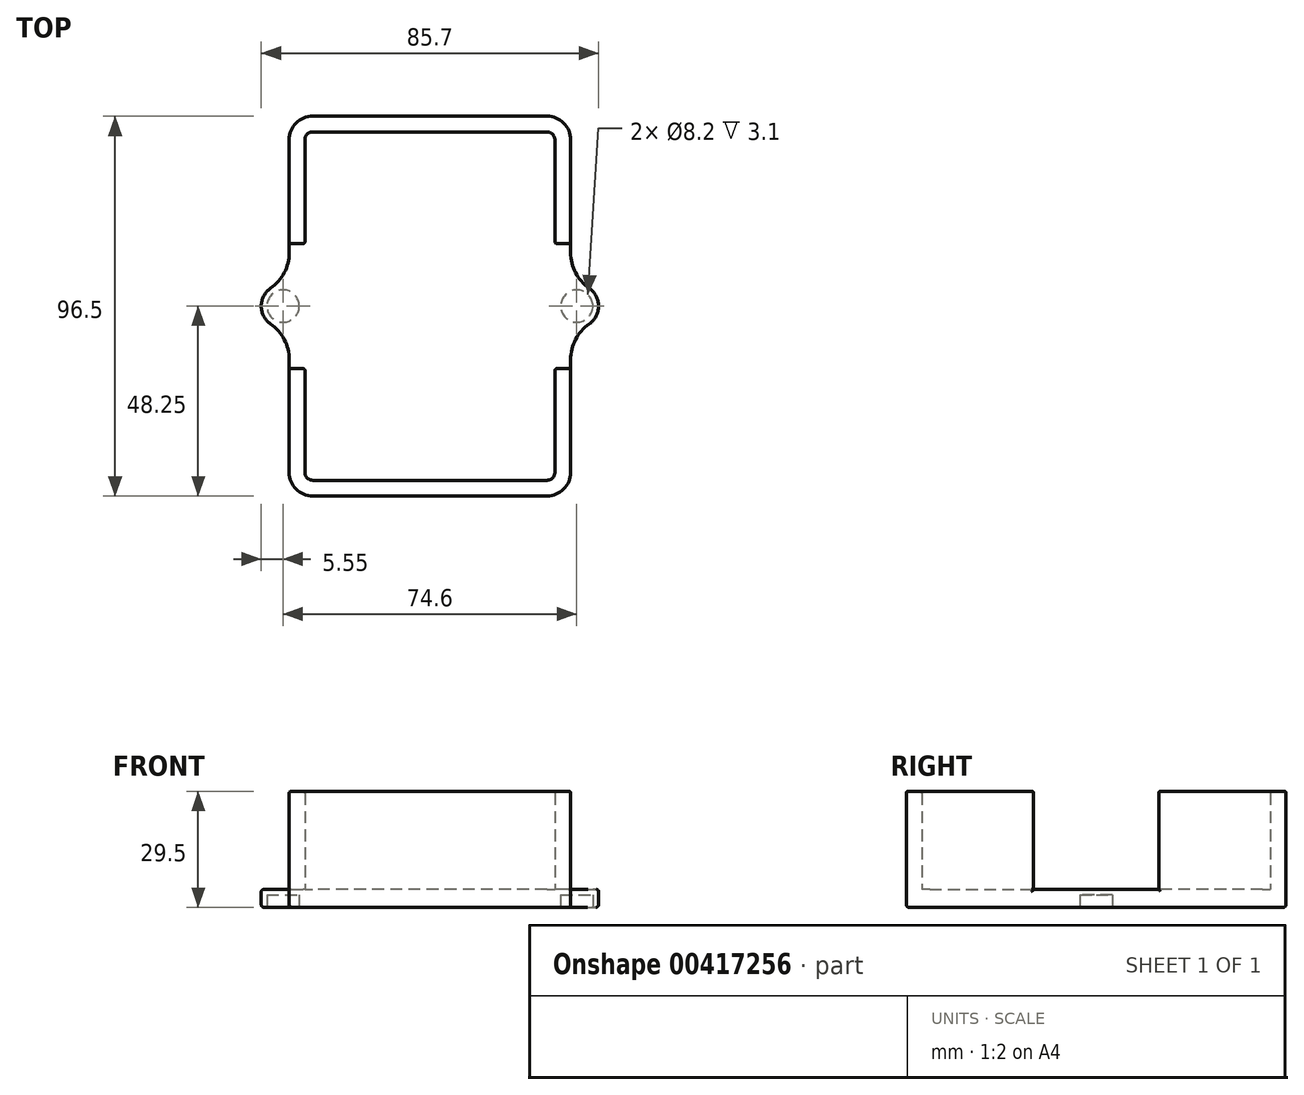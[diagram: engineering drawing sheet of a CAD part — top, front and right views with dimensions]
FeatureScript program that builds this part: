
annotation { "Feature Type Name" : "Feature", "Feature Type Description" : "" }
export const myFeature = defineFeature(function(context is Context, id is Id, definition is map)
    precondition{}
    {
        {
            var Q0;
            Q0=qCreatedBy(makeId("Top.planeOp"),FACE);
            var sketch = newSketch(context, id + "F0", { "sketchPlane" : qUnion([Q0])});
            skLineSegment(sketch, "E0", {"start": v(35.75, 42.25) * mm, "end": v(35.75, 13.59) * mm});
            skArc(sketch, "E1", {"start": v(35.75, 13.59) * mm, "mid": v(37, 8.5) * mm, "end": v(40.47, 4.56) * mm});
            skArc(sketch, "E2", {"start": v(40.47, 4.56) * mm, "mid": v(42.85, 0) * mm, "end": v(40.47, -4.56) * mm});
            skArc(sketch, "E3", {"start": v(40.47, -4.56) * mm, "mid": v(37, -8.5) * mm, "end": v(35.75, -13.59) * mm});
            skLineSegment(sketch, "E4", {"start": v(35.75, -13.59) * mm, "end": v(35.75, -42.25) * mm});
            skArc(sketch, "E5", {"start": v(35.75, -42.25) * mm, "mid": v(34, -46.5) * mm, "end": v(29.75, -48.25) * mm});
            skLineSegment(sketch, "E6", {"start": v(29.75, -48.25) * mm, "end": v(-29.75, -48.25) * mm});
            skArc(sketch, "E7", {"start": v(-29.75, -48.25) * mm, "mid": v(-34, -46.5) * mm, "end": v(-35.75, -42.25) * mm});
            skLineSegment(sketch, "E8", {"start": v(-35.75, -42.25) * mm, "end": v(-35.75, -13.59) * mm});
            skArc(sketch, "E9", {"start": v(-35.75, -13.59) * mm, "mid": v(-37, -8.5) * mm, "end": v(-40.47, -4.56) * mm});
            skArc(sketch, "E10", {"start": v(-40.47, -4.56) * mm, "mid": v(-42.85, 0) * mm, "end": v(-40.47, 4.56) * mm});
            skArc(sketch, "E11", {"start": v(-40.47, 4.56) * mm, "mid": v(-37, 8.5) * mm, "end": v(-35.75, 13.59) * mm});
            skLineSegment(sketch, "E12", {"start": v(-35.75, 13.59) * mm, "end": v(-35.75, 42.25) * mm});
            skArc(sketch, "E13", {"start": v(-35.75, 42.25) * mm, "mid": v(-34, 46.5) * mm, "end": v(-29.75, 48.25) * mm});
            skLineSegment(sketch, "E14", {"start": v(-29.75, 48.25) * mm, "end": v(29.75, 48.25) * mm});
            skArc(sketch, "E15", {"start": v(29.75, 48.25) * mm, "mid": v(34, 46.5) * mm, "end": v(35.75, 42.25) * mm});
            skSolve(sketch);
        }
        {
            var Q0;
            Q0=qSketchRegion(id+"F0",true);
            extrude(context, id + "F1", {"entities" : qUnion([Q0]), "depth" : 4.5 * mm});
        }
        {
            var Q0;
            Q0=makeQuery(id+"F1.opExtrude","CAP_FACE",FACE,{"disambiguationData":[OSD([sQuery(id+"F0.wireOp",EDGE,"E0"),sQuery(id+"F0.wireOp",EDGE,"E1"),sQuery(id+"F0.wireOp",EDGE,"E2"),sQuery(id+"F0.wireOp",EDGE,"E3"),sQuery(id+"F0.wireOp",EDGE,"E4"),sQuery(id+"F0.wireOp",EDGE,"E5"),sQuery(id+"F0.wireOp",EDGE,"E6"),sQuery(id+"F0.wireOp",EDGE,"E7"),sQuery(id+"F0.wireOp",EDGE,"E8"),sQuery(id+"F0.wireOp",EDGE,"E9"),sQuery(id+"F0.wireOp",EDGE,"E10"),sQuery(id+"F0.wireOp",EDGE,"E11"),sQuery(id+"F0.wireOp",EDGE,"E12"),sQuery(id+"F0.wireOp",EDGE,"E13"),sQuery(id+"F0.wireOp",EDGE,"E14"),sQuery(id+"F0.wireOp",EDGE,"E15")])],"isStart":true});
            var sketch = newSketch(context, id + "F2", { "sketchPlane" : qUnion([Q0])});
            skCircle(sketch, "E16", {"center": v(-37.3, 0) * mm, "radius": 4.1 * mm});
            skCircle(sketch, "E17", {"center": v(37.3, 0) * mm, "radius": 4.1 * mm});
            skSolve(sketch);
        }
        {
            var Q0;
            Q0=qSketchRegion(id+"F2",true);
            extrude(context, id + "F3", {"entities" : qUnion([Q0]), "operationType" : NewBodyOperationType.REMOVE, "oppositeDirection" : true, "depth" : 3.1 * mm});
        }
        {
            var Q0;
            Q0=makeQuery(id+"F1.opExtrude","CAP_FACE",FACE,{"disambiguationData":[OSD([sQuery(id+"F0.wireOp",EDGE,"E0"),sQuery(id+"F0.wireOp",EDGE,"E1"),sQuery(id+"F0.wireOp",EDGE,"E2"),sQuery(id+"F0.wireOp",EDGE,"E3"),sQuery(id+"F0.wireOp",EDGE,"E4"),sQuery(id+"F0.wireOp",EDGE,"E5"),sQuery(id+"F0.wireOp",EDGE,"E6"),sQuery(id+"F0.wireOp",EDGE,"E7"),sQuery(id+"F0.wireOp",EDGE,"E8"),sQuery(id+"F0.wireOp",EDGE,"E9"),sQuery(id+"F0.wireOp",EDGE,"E10"),sQuery(id+"F0.wireOp",EDGE,"E11"),sQuery(id+"F0.wireOp",EDGE,"E12"),sQuery(id+"F0.wireOp",EDGE,"E13"),sQuery(id+"F0.wireOp",EDGE,"E14"),sQuery(id+"F0.wireOp",EDGE,"E15")])],"isStart":false});
            var sketch = newSketch(context, id + "F4", { "sketchPlane" : qUnion([Q0])});
            skArc(sketch, "E18", {"start": v(-35.75, 16.39) * mm, "mid": v(-35.6, 16.03) * mm, "end": v(-35.25, 15.89) * mm});
            skLineSegment(sketch, "E19", {"start": v(-35.25, 15.89) * mm, "end": v(-32.25, 15.89) * mm});
            skArc(sketch, "E20", {"start": v(-32.25, 15.89) * mm, "mid": v(-31.9, 16.03) * mm, "end": v(-31.75, 16.39) * mm});
            skLineSegment(sketch, "E21", {"start": v(-31.75, 16.39) * mm, "end": v(-31.75, 42.25) * mm});
            skArc(sketch, "E22", {"start": v(-31.75, 42.25) * mm, "mid": v(-31.16, 43.66) * mm, "end": v(-29.75, 44.25) * mm});
            skLineSegment(sketch, "E23", {"start": v(-29.75, 44.25) * mm, "end": v(29.75, 44.25) * mm});
            skArc(sketch, "E24", {"start": v(29.75, 44.25) * mm, "mid": v(31.16, 43.66) * mm, "end": v(31.75, 42.25) * mm});
            skLineSegment(sketch, "E25", {"start": v(31.75, 42.25) * mm, "end": v(31.75, 16.39) * mm});
            skArc(sketch, "E26", {"start": v(31.75, 16.39) * mm, "mid": v(31.9, 16.03) * mm, "end": v(32.25, 15.89) * mm});
            skLineSegment(sketch, "E27", {"start": v(32.25, 15.89) * mm, "end": v(35.25, 15.89) * mm});
            skArc(sketch, "E28", {"start": v(35.25, 15.89) * mm, "mid": v(35.6, 16.03) * mm, "end": v(35.75, 16.39) * mm});
            skLineSegment(sketch, "E29", {"start": v(35.75, 16.39) * mm, "end": v(35.75, 42.25) * mm});
            skArc(sketch, "E30", {"start": v(35.75, 42.25) * mm, "mid": v(34, 46.5) * mm, "end": v(29.75, 48.25) * mm});
            skLineSegment(sketch, "E31", {"start": v(29.75, 48.25) * mm, "end": v(-29.75, 48.25) * mm});
            skArc(sketch, "E32", {"start": v(-29.75, 48.25) * mm, "mid": v(-34, 46.5) * mm, "end": v(-35.75, 42.25) * mm});
            skLineSegment(sketch, "E33", {"start": v(-35.75, 42.25) * mm, "end": v(-35.75, 16.39) * mm});
            skArc(sketch, "E34", {"start": v(35.75, -16.39) * mm, "mid": v(35.6, -16.03) * mm, "end": v(35.25, -15.89) * mm});
            skLineSegment(sketch, "E35", {"start": v(35.25, -15.89) * mm, "end": v(32.25, -15.89) * mm});
            skArc(sketch, "E36", {"start": v(32.25, -15.89) * mm, "mid": v(31.9, -16.03) * mm, "end": v(31.75, -16.39) * mm});
            skLineSegment(sketch, "E37", {"start": v(31.75, -16.39) * mm, "end": v(31.75, -42.25) * mm});
            skArc(sketch, "E38", {"start": v(31.75, -42.25) * mm, "mid": v(31.16, -43.66) * mm, "end": v(29.75, -44.25) * mm});
            skLineSegment(sketch, "E39", {"start": v(29.75, -44.25) * mm, "end": v(-29.75, -44.25) * mm});
            skArc(sketch, "E40", {"start": v(-29.75, -44.25) * mm, "mid": v(-31.16, -43.66) * mm, "end": v(-31.75, -42.25) * mm});
            skLineSegment(sketch, "E41", {"start": v(-31.75, -42.25) * mm, "end": v(-31.75, -16.39) * mm});
            skArc(sketch, "E42", {"start": v(-31.75, -16.39) * mm, "mid": v(-31.9, -16.03) * mm, "end": v(-32.25, -15.89) * mm});
            skLineSegment(sketch, "E43", {"start": v(-32.25, -15.89) * mm, "end": v(-35.25, -15.89) * mm});
            skArc(sketch, "E44", {"start": v(-35.25, -15.89) * mm, "mid": v(-35.6, -16.03) * mm, "end": v(-35.75, -16.39) * mm});
            skLineSegment(sketch, "E45", {"start": v(-35.75, -16.39) * mm, "end": v(-35.75, -42.25) * mm});
            skArc(sketch, "E46", {"start": v(-35.75, -42.25) * mm, "mid": v(-34, -46.5) * mm, "end": v(-29.75, -48.25) * mm});
            skLineSegment(sketch, "E47", {"start": v(-29.75, -48.25) * mm, "end": v(29.75, -48.25) * mm});
            skArc(sketch, "E48", {"start": v(29.75, -48.25) * mm, "mid": v(34, -46.5) * mm, "end": v(35.75, -42.25) * mm});
            skLineSegment(sketch, "E49", {"start": v(35.75, -42.25) * mm, "end": v(35.75, -16.39) * mm});
            skSolve(sketch);
        }
        {
            var Q0;
            Q0=qSketchRegion(id+"F4",true);
            extrude(context, id + "F5", {"entities" : qUnion([Q0]), "operationType" : NewBodyOperationType.ADD, "depth" : 25 * mm});
        }
        {
            var Q0;
            Q0=makeQuery(id+"F1.opExtrude","CAP_EDGE",EDGE,{"disambiguationData":[OSD([sQuery(id+"F0.wireOp",EDGE,"E14")])],"isStart":true});
            var Q1;
            Q1=makeQuery(id+"F1.opExtrude","CAP_EDGE",EDGE,{"disambiguationData":[OSD([sQuery(id+"F0.wireOp",EDGE,"E13")])],"isStart":true});
            var Q2;
            Q2=makeQuery(id+"F1.opExtrude","CAP_EDGE",EDGE,{"disambiguationData":[OSD([sQuery(id+"F0.wireOp",EDGE,"E12")])],"isStart":true});
            var Q3;
            Q3=makeQuery(id+"F1.opExtrude","CAP_EDGE",EDGE,{"disambiguationData":[OSD([sQuery(id+"F0.wireOp",EDGE,"E11")])],"isStart":true});
            var Q4;
            Q4=makeQuery(id+"F1.opExtrude","CAP_EDGE",EDGE,{"disambiguationData":[OSD([sQuery(id+"F0.wireOp",EDGE,"E10")])],"isStart":true});
            var Q5;
            Q5=makeQuery(id+"F1.opExtrude","CAP_EDGE",EDGE,{"disambiguationData":[OSD([sQuery(id+"F0.wireOp",EDGE,"E9")])],"isStart":true});
            var Q6;
            Q6=makeQuery(id+"F1.opExtrude","CAP_EDGE",EDGE,{"disambiguationData":[OSD([sQuery(id+"F0.wireOp",EDGE,"E8")])],"isStart":true});
            var Q7;
            Q7=makeQuery(id+"F1.opExtrude","CAP_EDGE",EDGE,{"disambiguationData":[OSD([sQuery(id+"F0.wireOp",EDGE,"E7")])],"isStart":true});
            var Q8;
            Q8=makeQuery(id+"F1.opExtrude","CAP_EDGE",EDGE,{"disambiguationData":[OSD([sQuery(id+"F0.wireOp",EDGE,"E6")])],"isStart":true});
            var Q9;
            Q9=makeQuery(id+"F1.opExtrude","CAP_EDGE",EDGE,{"disambiguationData":[OSD([sQuery(id+"F0.wireOp",EDGE,"E5")])],"isStart":true});
            var Q10;
            Q10=makeQuery(id+"F1.opExtrude","CAP_EDGE",EDGE,{"disambiguationData":[OSD([sQuery(id+"F0.wireOp",EDGE,"E4")])],"isStart":true});
            var Q11;
            Q11=makeQuery(id+"F1.opExtrude","CAP_EDGE",EDGE,{"disambiguationData":[OSD([sQuery(id+"F0.wireOp",EDGE,"E3")])],"isStart":true});
            var Q12;
            Q12=makeQuery(id+"F1.opExtrude","CAP_EDGE",EDGE,{"disambiguationData":[OSD([sQuery(id+"F0.wireOp",EDGE,"E2")])],"isStart":true});
            var Q13;
            Q13=makeQuery(id+"F1.opExtrude","CAP_EDGE",EDGE,{"disambiguationData":[OSD([sQuery(id+"F0.wireOp",EDGE,"E1")])],"isStart":true});
            var Q14;
            Q14=makeQuery(id+"F1.opExtrude","CAP_EDGE",EDGE,{"disambiguationData":[OSD([sQuery(id+"F0.wireOp",EDGE,"E0")])],"isStart":true});
            var Q15;
            Q15=makeQuery(id+"F1.opExtrude","CAP_EDGE",EDGE,{"disambiguationData":[OSD([sQuery(id+"F0.wireOp",EDGE,"E15")])],"isStart":true});
            fillet(context, id + "F6", {"entities" : qUnion([Q0, Q1, Q2, Q3, Q4, Q5, Q6, Q7, Q8, Q9, Q10, Q11, Q12, Q13, Q14, Q15]), "radius" : .7 * mm, "tangentPropagation" : true, "allowEdgeOverflow" : false});
        }
        {
            var Q0;
            Q0=makeQuery(id+"F5.opExtrude","CAP_EDGE",EDGE,{"disambiguationData":[OSD([sQuery(id+"F4.wireOp",EDGE,"E43")])],"isStart":false});
            var Q1;
            Q1=makeQuery(id+"F5.opExtrude","CAP_EDGE",EDGE,{"disambiguationData":[OSD([sQuery(id+"F4.wireOp",EDGE,"E42")])],"isStart":false});
            var Q2;
            Q2=makeQuery(id+"F5.opExtrude","CAP_EDGE",EDGE,{"disambiguationData":[OSD([sQuery(id+"F4.wireOp",EDGE,"E41")])],"isStart":false});
            var Q3;
            Q3=makeQuery(id+"F5.opExtrude","CAP_EDGE",EDGE,{"disambiguationData":[OSD([sQuery(id+"F4.wireOp",EDGE,"E44")])],"isStart":false});
            var Q4;
            Q4=makeQuery(id+"F5.opExtrude","CAP_EDGE",EDGE,{"disambiguationData":[OSD([sQuery(id+"F4.wireOp",EDGE,"E45")])],"isStart":false});
            var Q5;
            Q5=makeQuery(id+"F5.opExtrude","CAP_EDGE",EDGE,{"disambiguationData":[OSD([sQuery(id+"F4.wireOp",EDGE,"E46")])],"isStart":false});
            var Q6;
            Q6=makeQuery(id+"F5.opExtrude","CAP_EDGE",EDGE,{"disambiguationData":[OSD([sQuery(id+"F4.wireOp",EDGE,"E40")])],"isStart":false});
            var Q7;
            Q7=makeQuery(id+"F5.opExtrude","CAP_EDGE",EDGE,{"disambiguationData":[OSD([sQuery(id+"F4.wireOp",EDGE,"E39")])],"isStart":false});
            var Q8;
            Q8=makeQuery(id+"F5.opExtrude","CAP_EDGE",EDGE,{"disambiguationData":[OSD([sQuery(id+"F4.wireOp",EDGE,"E47")])],"isStart":false});
            var Q9;
            Q9=makeQuery(id+"F5.opExtrude","CAP_EDGE",EDGE,{"disambiguationData":[OSD([sQuery(id+"F4.wireOp",EDGE,"E48")])],"isStart":false});
            var Q10;
            Q10=makeQuery(id+"F5.opExtrude","CAP_EDGE",EDGE,{"disambiguationData":[OSD([sQuery(id+"F4.wireOp",EDGE,"E38")])],"isStart":false});
            var Q11;
            Q11=makeQuery(id+"F5.opExtrude","CAP_EDGE",EDGE,{"disambiguationData":[OSD([sQuery(id+"F4.wireOp",EDGE,"E37")])],"isStart":false});
            var Q12;
            Q12=makeQuery(id+"F5.opExtrude","CAP_EDGE",EDGE,{"disambiguationData":[OSD([sQuery(id+"F4.wireOp",EDGE,"E49")])],"isStart":false});
            var Q13;
            Q13=makeQuery(id+"F5.opExtrude","CAP_EDGE",EDGE,{"disambiguationData":[OSD([sQuery(id+"F4.wireOp",EDGE,"E34")])],"isStart":false});
            var Q14;
            Q14=makeQuery(id+"F5.opExtrude","CAP_EDGE",EDGE,{"disambiguationData":[OSD([sQuery(id+"F4.wireOp",EDGE,"E35")])],"isStart":false});
            var Q15;
            Q15=makeQuery(id+"F5.opExtrude","CAP_EDGE",EDGE,{"disambiguationData":[OSD([sQuery(id+"F4.wireOp",EDGE,"E36")])],"isStart":false});
            var Q16;
            Q16=makeQuery(id+"F5.opExtrude","CAP_EDGE",EDGE,{"disambiguationData":[OSD([sQuery(id+"F4.wireOp",EDGE,"E27")])],"isStart":false});
            var Q17;
            Q17=makeQuery(id+"F5.opExtrude","CAP_EDGE",EDGE,{"disambiguationData":[OSD([sQuery(id+"F4.wireOp",EDGE,"E26")])],"isStart":false});
            var Q18;
            Q18=makeQuery(id+"F5.opExtrude","CAP_EDGE",EDGE,{"disambiguationData":[OSD([sQuery(id+"F4.wireOp",EDGE,"E25")])],"isStart":false});
            var Q19;
            Q19=makeQuery(id+"F5.opExtrude","CAP_EDGE",EDGE,{"disambiguationData":[OSD([sQuery(id+"F4.wireOp",EDGE,"E28")])],"isStart":false});
            var Q20;
            Q20=makeQuery(id+"F5.opExtrude","CAP_EDGE",EDGE,{"disambiguationData":[OSD([sQuery(id+"F4.wireOp",EDGE,"E29")])],"isStart":false});
            var Q21;
            Q21=makeQuery(id+"F5.opExtrude","CAP_EDGE",EDGE,{"disambiguationData":[OSD([sQuery(id+"F4.wireOp",EDGE,"E30")])],"isStart":false});
            var Q22;
            Q22=makeQuery(id+"F5.opExtrude","CAP_EDGE",EDGE,{"disambiguationData":[OSD([sQuery(id+"F4.wireOp",EDGE,"E24")])],"isStart":false});
            var Q23;
            Q23=makeQuery(id+"F5.opExtrude","CAP_EDGE",EDGE,{"disambiguationData":[OSD([sQuery(id+"F4.wireOp",EDGE,"E23")])],"isStart":false});
            var Q24;
            Q24=makeQuery(id+"F5.opExtrude","CAP_EDGE",EDGE,{"disambiguationData":[OSD([sQuery(id+"F4.wireOp",EDGE,"E31")])],"isStart":false});
            var Q25;
            Q25=makeQuery(id+"F5.opExtrude","CAP_EDGE",EDGE,{"disambiguationData":[OSD([sQuery(id+"F4.wireOp",EDGE,"E22")])],"isStart":false});
            var Q26;
            Q26=makeQuery(id+"F5.opExtrude","CAP_EDGE",EDGE,{"disambiguationData":[OSD([sQuery(id+"F4.wireOp",EDGE,"E32")])],"isStart":false});
            var Q27;
            Q27=makeQuery(id+"F5.opExtrude","CAP_EDGE",EDGE,{"disambiguationData":[OSD([sQuery(id+"F4.wireOp",EDGE,"E33")])],"isStart":false});
            var Q28;
            Q28=makeQuery(id+"F5.opExtrude","CAP_EDGE",EDGE,{"disambiguationData":[OSD([sQuery(id+"F4.wireOp",EDGE,"E21")])],"isStart":false});
            var Q29;
            Q29=makeQuery(id+"F5.opExtrude","CAP_EDGE",EDGE,{"disambiguationData":[OSD([sQuery(id+"F4.wireOp",EDGE,"E20")])],"isStart":false});
            var Q30;
            Q30=makeQuery(id+"F5.opExtrude","CAP_EDGE",EDGE,{"disambiguationData":[OSD([sQuery(id+"F4.wireOp",EDGE,"E19")])],"isStart":false});
            var Q31;
            Q31=makeQuery(id+"F5.opExtrude","CAP_EDGE",EDGE,{"disambiguationData":[OSD([sQuery(id+"F4.wireOp",EDGE,"E18")])],"isStart":false});
            fillet(context, id + "F7", {"entities" : qUnion([Q0, Q1, Q2, Q3, Q4, Q5, Q6, Q7, Q8, Q9, Q10, Q11, Q12, Q13, Q14, Q15, Q16, Q17, Q18, Q19, Q20, Q21, Q22, Q23, Q24, Q25, Q26, Q27, Q28, Q29, Q30, Q31]), "radius" : .5 * mm, "tangentPropagation" : true, "allowEdgeOverflow" : false});
        }
        {
            var Q0;
            Q0=makeQuery(id+"F1.opExtrude","CAP_EDGE",EDGE,{"disambiguationData":[OSD([sQuery(id+"F0.wireOp",EDGE,"E3")])],"isStart":false});
            var Q1;
            Q1=makeQuery(id+"F1.opExtrude","CAP_EDGE",EDGE,{"disambiguationData":[OSD([sQuery(id+"F0.wireOp",EDGE,"E2")])],"isStart":false});
            var Q2;
            Q2=makeQuery(id+"F1.opExtrude","CAP_EDGE",EDGE,{"disambiguationData":[OSD([sQuery(id+"F0.wireOp",EDGE,"E1")])],"isStart":false});
            var Q3;
            Q3=makeQuery(id+"F1.opExtrude","CAP_EDGE",EDGE,{"disambiguationData":[OSD([sQuery(id+"F0.wireOp",EDGE,"E4")])],"isStart":false});
            var Q4;
            Q4=makeQuery(id+"F1.opExtrude","CAP_EDGE",EDGE,{"disambiguationData":[OSD([sQuery(id+"F0.wireOp",EDGE,"E0")])],"isStart":false});
            fillet(context, id + "F8", {"entities" : qUnion([Q0, Q1, Q2, Q3, Q4]), "radius" : .5 * mm, "tangentPropagation" : true, "allowEdgeOverflow" : false});
        }
        {
            var Q0;
            Q0=makeQuery(id+"F1.opExtrude","CAP_EDGE",EDGE,{"disambiguationData":[OSD([sQuery(id+"F0.wireOp",EDGE,"E8")])],"isStart":false});
            var Q1;
            Q1=makeQuery(id+"F1.opExtrude","CAP_EDGE",EDGE,{"disambiguationData":[OSD([sQuery(id+"F0.wireOp",EDGE,"E9")])],"isStart":false});
            var Q2;
            Q2=makeQuery(id+"F1.opExtrude","CAP_EDGE",EDGE,{"disambiguationData":[OSD([sQuery(id+"F0.wireOp",EDGE,"E10")])],"isStart":false});
            var Q3;
            Q3=makeQuery(id+"F1.opExtrude","CAP_EDGE",EDGE,{"disambiguationData":[OSD([sQuery(id+"F0.wireOp",EDGE,"E12")])],"isStart":false});
            var Q4;
            Q4=makeQuery(id+"F1.opExtrude","CAP_EDGE",EDGE,{"disambiguationData":[OSD([sQuery(id+"F0.wireOp",EDGE,"E11")])],"isStart":false});
            fillet(context, id + "F9", {"entities" : qUnion([Q0, Q1, Q2, Q3, Q4]), "radius" : .5 * mm, "tangentPropagation" : true, "allowEdgeOverflow" : false});
        }
        {
            var Q0;
            Q0=makeQuery(id+"F1.opExtrude","CAP_FACE",FACE,{"disambiguationData":[OSD([sQuery(id+"F0.wireOp",EDGE,"E0"),sQuery(id+"F0.wireOp",EDGE,"E1"),sQuery(id+"F0.wireOp",EDGE,"E2"),sQuery(id+"F0.wireOp",EDGE,"E3"),sQuery(id+"F0.wireOp",EDGE,"E4"),sQuery(id+"F0.wireOp",EDGE,"E5"),sQuery(id+"F0.wireOp",EDGE,"E6"),sQuery(id+"F0.wireOp",EDGE,"E7"),sQuery(id+"F0.wireOp",EDGE,"E8"),sQuery(id+"F0.wireOp",EDGE,"E9"),sQuery(id+"F0.wireOp",EDGE,"E10"),sQuery(id+"F0.wireOp",EDGE,"E11"),sQuery(id+"F0.wireOp",EDGE,"E12"),sQuery(id+"F0.wireOp",EDGE,"E13"),sQuery(id+"F0.wireOp",EDGE,"E14"),sQuery(id+"F0.wireOp",EDGE,"E15")])],"isStart":false});
            var sketch = newSketch(context, id + "F10", { "sketchPlane" : qUnion([Q0])});
            skCircle(sketch, "E50", {"center": v(0, 0) * mm, "radius": 10.19 * mm});
            skSolve(sketch);
        }
        {
            var Q0;
            Q0=makeQuery(id+"F10.imprint","IMPRINT",FACE,{"disambiguationData":[TD([[makeQuery(id+"F10.imprint","IMPRINT",EDGE,{"derivedFrom":sQuery(id+"F10.wireOp",EDGE,"E50")}),1.0]])]});
            var Q1;
            Q1=sQuery(id+"F10.wireOp",EDGE,"E50");
            extrude(context, id + "F11", {"entities" : qUnion([Q0]), "operationType" : NewBodyOperationType.REMOVE, "surfaceEntities" : qUnion([Q1]), "depth" : 25 * mm});
        }
    });
